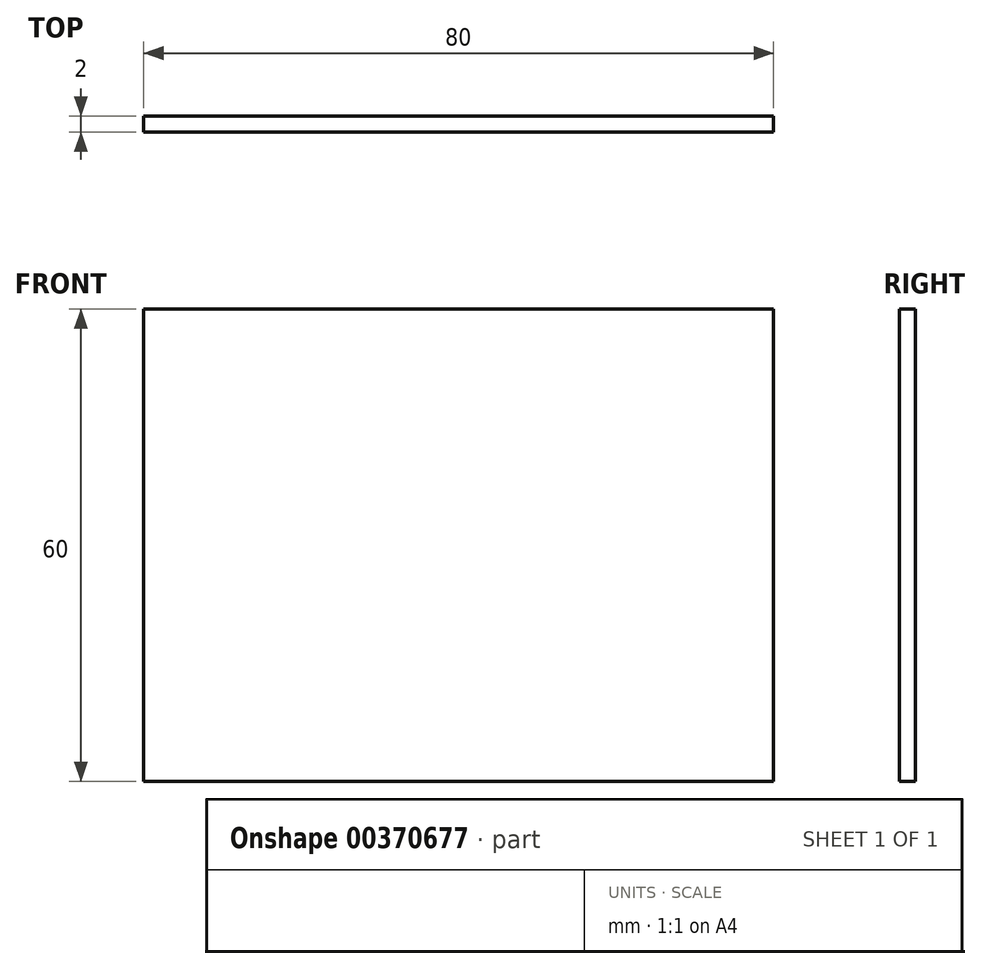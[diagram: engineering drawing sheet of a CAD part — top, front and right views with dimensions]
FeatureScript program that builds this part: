
annotation { "Feature Type Name" : "Feature", "Feature Type Description" : "" }
export const myFeature = defineFeature(function(context is Context, id is Id, definition is map)
    precondition{}
    {
        {
            var Q0;
            Q0=qCreatedBy(makeId("Front.planeOp"),FACE);
            var sketch = newSketch(context, id + "F0", { "sketchPlane" : qUnion([Q0])});
            skLineSegment(sketch, "E0.bottom", {"start": v(40, -30) * mm, "end": v(-40, -30) * mm});
            skLineSegment(sketch, "E0.top", {"start": v(40, 30) * mm, "end": v(-40, 30) * mm});
            skLineSegment(sketch, "E0.left", {"start": v(40, -30) * mm, "end": v(40, 30) * mm});
            skLineSegment(sketch, "E0.right", {"start": v(-40, -30) * mm, "end": v(-40, 30) * mm});
            skPoint(sketch, "E0.middle", {"position": v(0, 0) * mm});
            skSolve(sketch);
        }
        {
            var Q0;
            Q0 = qSketchRegion(id + "F0", true);
            extrude(context, id + "F1", {"entities" : qUnion([Q0]), "depth" : 2 * mm});
        }
    });
